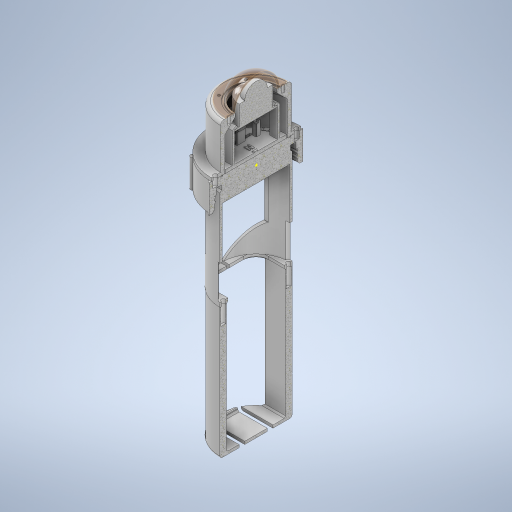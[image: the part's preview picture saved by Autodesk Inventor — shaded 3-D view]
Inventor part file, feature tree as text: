
AUTODESK INVENTOR PART (.ipt)
format: ipt  version: 2023 (Build 270158000, 158)  size: 2,586,112 bytes
history: native  units: in
note: dims shown in document units (in); Inventor stores cm internally (conversion verified against a paired STEP export)
features: extrude x56, sketch x46, projected_geometry x18, mirror x9, other x8, fillet x7, chamfer x7, pattern_circular x3, plane x3, helix x1
ambient origin geometry x8: Origin, YZ Plane, XZ Plane, XY Plane, X Axis, Y Axis, Z Axis, Center Point
bodies: Body1 (feature_tree), Body2 (feature_tree), Body3 (feature_tree), Body4 (feature_tree), Body5 (feature_tree), Body6 (feature_tree)
feature tree (158):
  other  "BatteryCage"
  sketch  "Sketch1"  dims[d0=2.5748in d1=0.0098in]
  extrude  "Start of Battery Cage"  Depth=0.0098in
  extrude  "Extrusion2"  Depth=0.4724in
  extrude  "Extrusion3"  Depth=0.0984in
  fillet  "Fillet1"  Radius=0.1969in
  chamfer  "Chamfer1"  Distance=0.0984in
  fillet  "Fillet2"  Radius=0.1181in
  extrude  "Extrusion4"  Depth=0.0197in
  chamfer  "Chamfer2"  Distance=0.0787in Angle=45.0deg
  sketch  "Sketch4"  dims[d4=0.0984in d5=0.0in d6=0.0079in d7=0.1969in]
  extrude  "Extrusion6"  Depth=4.4724in TaperAngle=0.0deg
  mirror  "Mirror1"
  extrude  "Battery Eject Hole"  Depth=0.0787in
  sketch  "Sketch6"  dims[d8=0.7874in]
  extrude  "Start of Pi Cage"  Depth=0.5906in TaperAngle=0.0deg
  extrude  "Extrusion9"  Depth=0.0512in
  chamfer  "Chamfer4"  Distance=0.0984in
  sketch  "Sketch9"  dims[d13=0.3937in d14=0.0in d15=0.0197in d16=0.0512in d17=0.0787in d18=45.0deg]
  extrude  "Extrusion10"  Depth=0.0787in TaperAngle=45.0deg
  extrude  "Shave Down for 40oz"  Depth=0.0984in
  fillet  "Battery Bottom Fillet"  Radius=2.0472in
  extrude  "Extrusion11"  Depth=2.9528in TaperAngle=0.0deg
  extrude  "Extrusion12"  Depth=0.5669in
  sketch  "Sketch11"  dims[d22=0.0512in d23=0.0787in d24=45.0deg d25=0.0512in]
  extrude  "Extrusion13"  Depth=0.8661in
  extrude  "Extrusion14"  Depth=0.0787in
  chamfer  "Chamfer5"  Distance=0.9843in
  extrude  "Extrusion15"  Depth=0.0787in TaperAngle=0.0deg
  sketch  "Sketch15"  dims[d36=0.0512in]
  extrude  "Extrusion17"  Depth=0.5906in
  extrude  "Extrusion18"  TaperAngle=0.0deg  [1 undecoded]
  extrude  "Extrusion19"  Depth=0.1122in
  pattern_circular  "Circular Pattern1"  Count=4 Angle=360.0deg
  extrude  "Extrusion20"  Depth=0.2756in TaperAngle=0.0deg
  pattern_circular  "Circular Pattern2"  Count=8 Angle=360.0deg
  sketch  "Sketch18"  dims[d41=0.1476in d42=0.0984in d43=0.0in]
  helix  "Coil1"  [1 undecoded]
  extrude  "Extrusion21"  Depth=0.1102in
  extrude  "Extrusion22"  Depth=0.0787in
  extrude  "Extrusion23"  Depth=0.3937in
  extrude  "Extrusion24"  Depth=0.3937in TaperAngle=0.0deg
  chamfer  "Chamfer6"  Distance=0.3937in
  extrude  "Tower O-ring Gland"  Depth=0.2756in
  extrude  "Sensor Tower Base"  Depth=0.0787in TaperAngle=45.0deg
  extrude  "Extrusion27"  TaperAngle=0.0deg  [1 undecoded]
  sketch  "Sketch23"  dims[d53=1.1811in d54=0.0in d55=0.5669in]
  extrude  "Extrusion28"  Depth=0.0787in
  sketch  "Sketch30"  dims[d61=0.0in]
  extrude  "Extrusion34"  Depth=0.0787in
  extrude  "Extrusion35"  Depth=0.0787in
  extrude  "Extrusion36"  TaperAngle=0.0deg  [1 undecoded]
  extrude  "North Indicator"  Depth=0.0787in
  extrude  "Extrusion37"  Depth=0.0787in
  extrude  "Extrusion38"  Depth=0.0787in
  mirror  "Mirror2"
  extrude  "Extrusion39"  Depth=0.0787in
  extrude  "Extrusion40"  Depth=0.0787in
  extrude  "Extrusion41"  TaperAngle=0.0deg  [1 undecoded]
  mirror  "Mirror3"
  extrude  "Extrusion56"  Depth=0.0787in
  mirror  "Mirror8"
  extrude  "Magnetometer Retaining Tab"  Depth=0.0787in
  extrude  "Retaining Tap Ramp"  Depth=0.0787in
  mirror  "Mirror Retaining Tab"
  extrude  "Start of Cover"  Depth=0.0787in
  extrude  "Extrusion30"  TaperAngle=0.0deg  [1 undecoded]
  sketch  "Sketch47"  dims[d89=0.1575in d90=0.2756in d91=0.0in d92=3.1496in d93=360.0deg d95=2.4016in]
  extrude  "Extrusion52"  Depth=0.0787in
  sketch  "Sketch48"  dims[d96=0.185in d97=0.1102in]
  plane  "Work Plane4"
  extrude  "Extrusion53"  Depth=0.0787in
  mirror  "Mirror4"
  mirror  "Mirror5"
  fillet  "Fillet7"  [1 undecoded]
  extrude  "Extrusion50"  Depth=0.0787in
  extrude  "Trim Pi Cage for 40oz"  Depth=0.0787in
  extrude  "Extrusion31"  TaperAngle=0.0deg  [1 undecoded]
  chamfer  "Chamfer7"  Distance=0.0787in Angle=45.0deg
  extrude  "Extrusion32"  Depth=0.0787in
  pattern_circular  "Circular Pattern3"  [2 undecoded]
  extrude  "Dome O-ring Gland"  Depth=0.0787in TaperAngle=0.0deg
  fillet  "Fillet4"  Radius=2.3622in
  plane  "Work Plane2"
  extrude  "Extrusion47"  Depth=0.0787in
  extrude  "Indexing tab"  Depth=0.0787in
  mirror  "Mirror6"
  chamfer  "Chamfer8"  Distance=0.0354in
  extrude  "Manufacturability: Sensor Cover Base"  Depth=0.0787in
  extrude  "North Marker External"  Depth=0.0787in TaperAngle=45.0deg
  extrude  "Start of Camera"  Depth=0.0787in
  fillet  "Fillet5"  Radius=1.0in
  sketch  "Sketch37"  dims[d74=0.5669in d75=0.0in]
  extrude  "Extrusion43"  Depth=0.0197in
  plane  "Work Plane1"
  extrude  "Extrusion45"  Depth=0.0787in
  extrude  "Extrusion46"  Depth=0.0787in
  fillet  "Fillet6"  Radius=0.3937in
  mirror  "Mirror7"
  other  "Start of Dome"
  sketch  "Sketch3"  dims[d2=2.0512in d3=0.4724in]
  projected_geometry  "Projected Loop1"
  projected_geometry  "Projected Loop2"
  other  "StartOfPiCage"
  other  "PiCage"
  sketch  "Sketch8"  dims[d9=0.1969in d10=0.0984in d11=0.0in d12=0.1181in]
  projected_geometry  "Projected Loop3"
  sketch  "Sketch10"  dims[d19=0.1181in d20=4.4724in d21=0.0in]
  sketch  "Sketch12"  dims[d31=0.1732in d32=0.5906in d33=0.0in]
  sketch  "Sketch14"  dims[d34=0.0512in d35=0.0512in]
  projected_geometry  "Projected Loop4"
  sketch  "Sketch16"  dims[d37=0.0in]
  sketch  "Sketch17"  dims[d38=0.0512in]
  sketch  "Sketch19"  dims[d44=0.0512in d45=0.0787in d46=45.0deg]
  projected_geometry  "Projected Loop5"
  sketch  "Sketch20"  dims[d47=0.0984in d48=0.0984in d49=2.0472in]
  other  "SensorTower"
  sketch  "Sketch22"  dims[d50=0.2756in d51=2.9528in d52=0.0in]
  other  "SensorCover"
  sketch  "Sketch26"  dims[d56=0.0in d57=0.8661in]
  sketch  "Sketch27"  dims[d58=0.0787in d59=0.6299in]
  sketch  "Sketch28"  dims[d60=0.0984in]
  sketch  "Sketch31"  dims[d62=0.1772in]
  sketch  "Sketch33"  dims[d63=0.2756in]
  projected_geometry  "Projected Loop7"
  sketch  "Sketch34"  dims[d64=0.0172in d65=0.9843in d66=0.0in]
  projected_geometry  "Projected Loop8"
  projected_geometry  "Projected Loop9"
  projected_geometry  "Projected Loop10"
  projected_geometry  "Projected Loop11"
  sketch  "Sketch35"  dims[d67=0.9843in d68=0.0787in d69=45.0deg d70=0.1969in d71=0.0in]
  projected_geometry  "Projected Loop12"
  sketch  "Sketch36"  dims[d72=0.7874in d73=0.5906in]
  other  "Camera"
  sketch  "Sketch38"  dims[d76=3.1181in d77=0.1122in]
  sketch  "Sketch39"  dims[d78=0.2756in]
  sketch  "Sketch40"  dims[d79=0.0in]
  sketch  "Sketch41"  dims[d80=0.7087in]
  sketch  "Sketch43"  dims[d81=0.0in]
  sketch  "Sketch44"  dims[d82=0.1732in]
  sketch  "Sketch45"  dims[d83=1.4173in]
  projected_geometry  "Projected Loop13"
  sketch  "Sketch46"  dims[d84=0.2362in d85=0.0in d86=1.5748in d87=360.0deg]
  projected_geometry  "Projected Loop14"
  projected_geometry  "Projected Loop15"
  sketch  "Sketch49"  dims[d98=0.0787in d99=1.4016in]
  sketch  "Sketch50"  dims[d100=0.1457in d101=0.3937in d102=0.9449in]
  sketch  "Sketch51"  dims[d103=0.0in d104=90.0deg d105=90.0deg d106=0.0in d107=0.0in d108=0.3937in d109=0.0in]
  sketch  "Sketch52"  dims[d110=0.2362in]
  projected_geometry  "Projected Loop16"
  other  "Clear Dome"
  sketch  "Sketch53"  dims[d111=0.0in d112=0.3937in d113=0.0in]
  projected_geometry  "Projected Loop17"
  sketch  "Sketch54"  dims[d114=0.2756in d115=0.2756in]
  projected_geometry  "Projected Loop18"
  sketch  "Sketch55"  dims[d116=0.3937in d117=0.0in d118=0.0768in d119=0.0787in d120=45.0deg]
  projected_geometry  "Projected Loop19"
  sketch  "Sketch56"  dims[d127=0.1181in d128=0.0in d129=2.126in d130=0.2953in d131=1.4173in d132=0.0in d133=1.4961in d134=1.3386in d135=0.0709in d136=0.1969in d137=0.9843in d138=0.0in d139=0.2756in d141=2.1654in d142=0.1575in d144=0.1181in d145=0.0in d146=0.1575in d147=1.4173in d148=0.0in d149=1.4567in d150=0.1181in d151=0.0in d152=0.3543in d153=0.0787in d154=45.0deg d155=0.9449in d156=0.0866in d157=0.2362in d158=0.0in d159=2.3622in d160=360.0deg d162=1.5748in d163=0.0669in d164=0.0354in d165=0.0in d167=0.1181in d168=0.0787in d169=0.0787in d170=45.0deg d171=1.0079in d172=1.0in d173=0.0197in d174=0.0591in d175=0.0591in d176=0.3937in d177=0.0in d178=0.4724in d179=0.0in d180=0.0787in d181=0.0787in d182=0.4724in d183=0.0in d184=0.2756in d185=0.5118in d186=0.0in d187=45.0deg d188=0.0591in d189=0.5512in d190=0.0in d191=0.0472in d192=30.0deg d193=0.0315in d194=0.0787in d195=0.0787in d196=0.0in d197=0.5512in d198=1.2008in d199=0.0in d200=0.063in d201=45.0deg d202=30.0deg d203=0.1181in d204=0.0945in d205=1.2008in d206=0.0in d207=1.4961in d208=0.0984in d209=0.063in d210=0.0in d211=0.0394in d212=1.1772in d213=0.689in d214=0.0in d215=0.0276in d216=0.0in d217=0.0787in d218=0.1378in d219=0.3937in d220=0.126in d221=0.0in d222=0.7835in d223=0.3937in d224=0.0in d225=0.3858in d229=-0.0236in d230=0.1772in d231=0.748in d232=0.3937in d233=0.0in d234=0.0197in d235=0.3937in d236=0.0in d237=0.1024in d238=0.0197in d239=0.0197in d240=0.3937in d241=0.0in d242=2.126in d243=0.1476in d244=2.1654in d245=0.1181in d246=0.0in d247=30.0deg d248=0.1575in d251=0.3937in d252=0.0in d253=45.0deg d254=0.1181in d255=0.1575in d256=0.0in d257=0.0394in d258=0.1378in d259=0.0in d260=2.4409in d261=2.3228in d262=0.0354in d263=0.0in d264=0.0787in d265=0.0787in d266=1.063in d267=0.3031in d268=1.6299in d269=0.0787in d270=360.0deg d271=0.0098in d272=0.0in d274=0.3782in d275=0.1683in d276=0.0787in d277=0.2756in d278=0.1378in d279=0.5118in d280=0.0in d281=0.0591in d282=0.0472in d283=30.0deg d284=45.0deg d285=0.0315in d286=0.5118in d287=0.0in d288=0.1458in d289=0.1378in d290=0.1181in d291=0.0in d292=0.2953in d293=0.2756in d294=0.0591in d295=0.0in]
note: 10 required parameter values undecoded (feature->parameter linkage not recoverable at this tier; creation-order binding heuristic only, values carry confidence <= 0.55)
